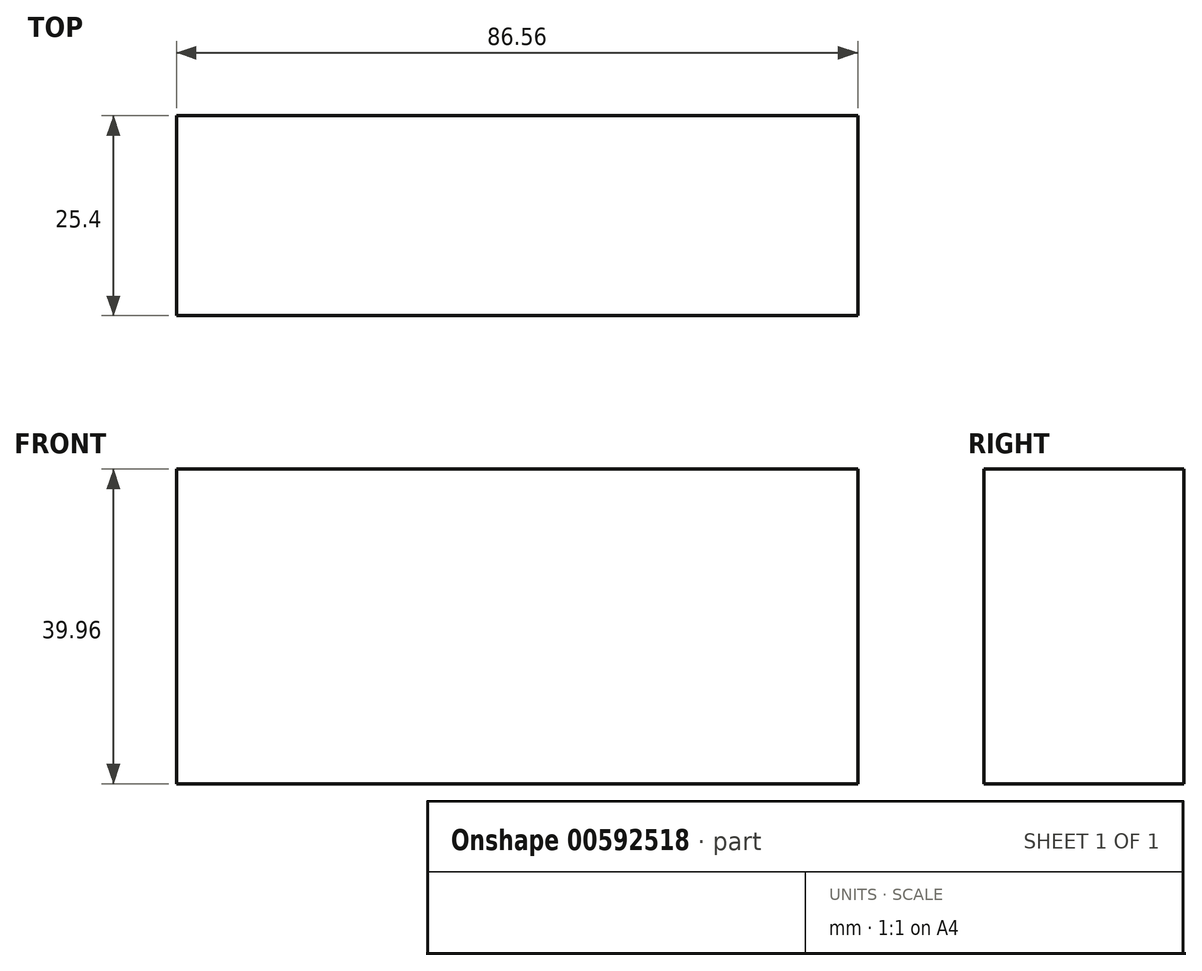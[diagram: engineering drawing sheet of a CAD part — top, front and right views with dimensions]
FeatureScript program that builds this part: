
annotation { "Feature Type Name" : "Feature", "Feature Type Description" : "" }
export const myFeature = defineFeature(function(context is Context, id is Id, definition is map)
    precondition{}
    {
        {
            var Q0;
            Q0=qCreatedBy(makeId("Front.planeOp"),FACE);
            var sketch = newSketch(context, id + "F0", { "sketchPlane" : qUnion([Q0])});
            skLineSegment(sketch, "E0.bottom", {"start": v(43.28, -19.98) * mm, "end": v(-43.28, -19.98) * mm});
            skLineSegment(sketch, "E0.top", {"start": v(43.28, 19.98) * mm, "end": v(-43.28, 19.98) * mm});
            skLineSegment(sketch, "E0.left", {"start": v(43.28, -19.98) * mm, "end": v(43.28, 19.98) * mm});
            skLineSegment(sketch, "E0.right", {"start": v(-43.28, -19.98) * mm, "end": v(-43.28, 19.98) * mm});
            skPoint(sketch, "E0.middle", {"position": v(0, 0) * mm});
            skSolve(sketch);
        }
        {
            var Q0;
            Q0=makeQuery(id+"F0.imprint","IMPRINT",FACE,{"disambiguationData":[TD([[makeQuery(id+"F0.imprint","IMPRINT",EDGE,{"derivedFrom":sQuery(id+"F0.wireOp",EDGE,"E0.bottom")}),-1.0]])]});
            extrude(context, id + "F1", {"entities" : qUnion([Q0]), "depth" : 25.4 * mm, "offsetDistance" : 25.4 * mm});
        }
    });
